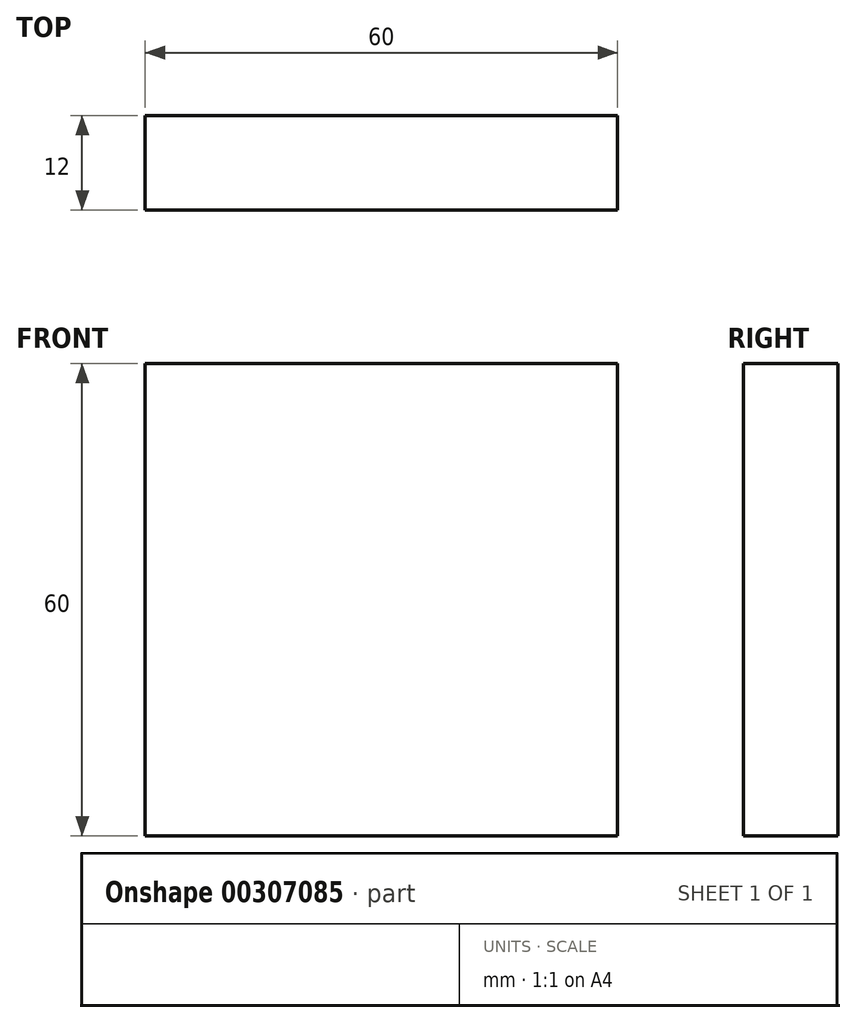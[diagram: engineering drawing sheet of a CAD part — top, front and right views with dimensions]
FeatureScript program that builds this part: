
annotation { "Feature Type Name" : "Feature", "Feature Type Description" : "" }
export const myFeature = defineFeature(function(context is Context, id is Id, definition is map)
    precondition{}
    {
        {
            var Q0;
            Q0=qCreatedBy(makeId("Front.planeOp"),FACE);
            var sketch = newSketch(context, id + "F0", { "sketchPlane" : qUnion([Q0])});
            skLineSegment(sketch, "E0.bottom", {"start": v(-23.87, 32.85) * mm, "end": v(36.13, 32.85) * mm});
            skLineSegment(sketch, "E0.top", {"start": v(-23.87, -27.15) * mm, "end": v(36.13, -27.15) * mm});
            skLineSegment(sketch, "E0.left", {"start": v(-23.87, 32.85) * mm, "end": v(-23.87, -27.15) * mm});
            skLineSegment(sketch, "E0.right", {"start": v(36.13, 32.85) * mm, "end": v(36.13, -27.15) * mm});
            skSolve(sketch);
        }
        {
            var Q0;
            Q0=makeQuery(id+"F0.imprint","IMPRINT",FACE,{"disambiguationData":[TD([[makeQuery(id+"F0.imprint","IMPRINT",EDGE,{"derivedFrom":sQuery(id+"F0.wireOp",EDGE,"E0.bottom")}),-1.0]])]});
            extrude(context, id + "F1", {"entities" : qUnion([Q0]), "depth" : 12 * mm});
        }
    });
